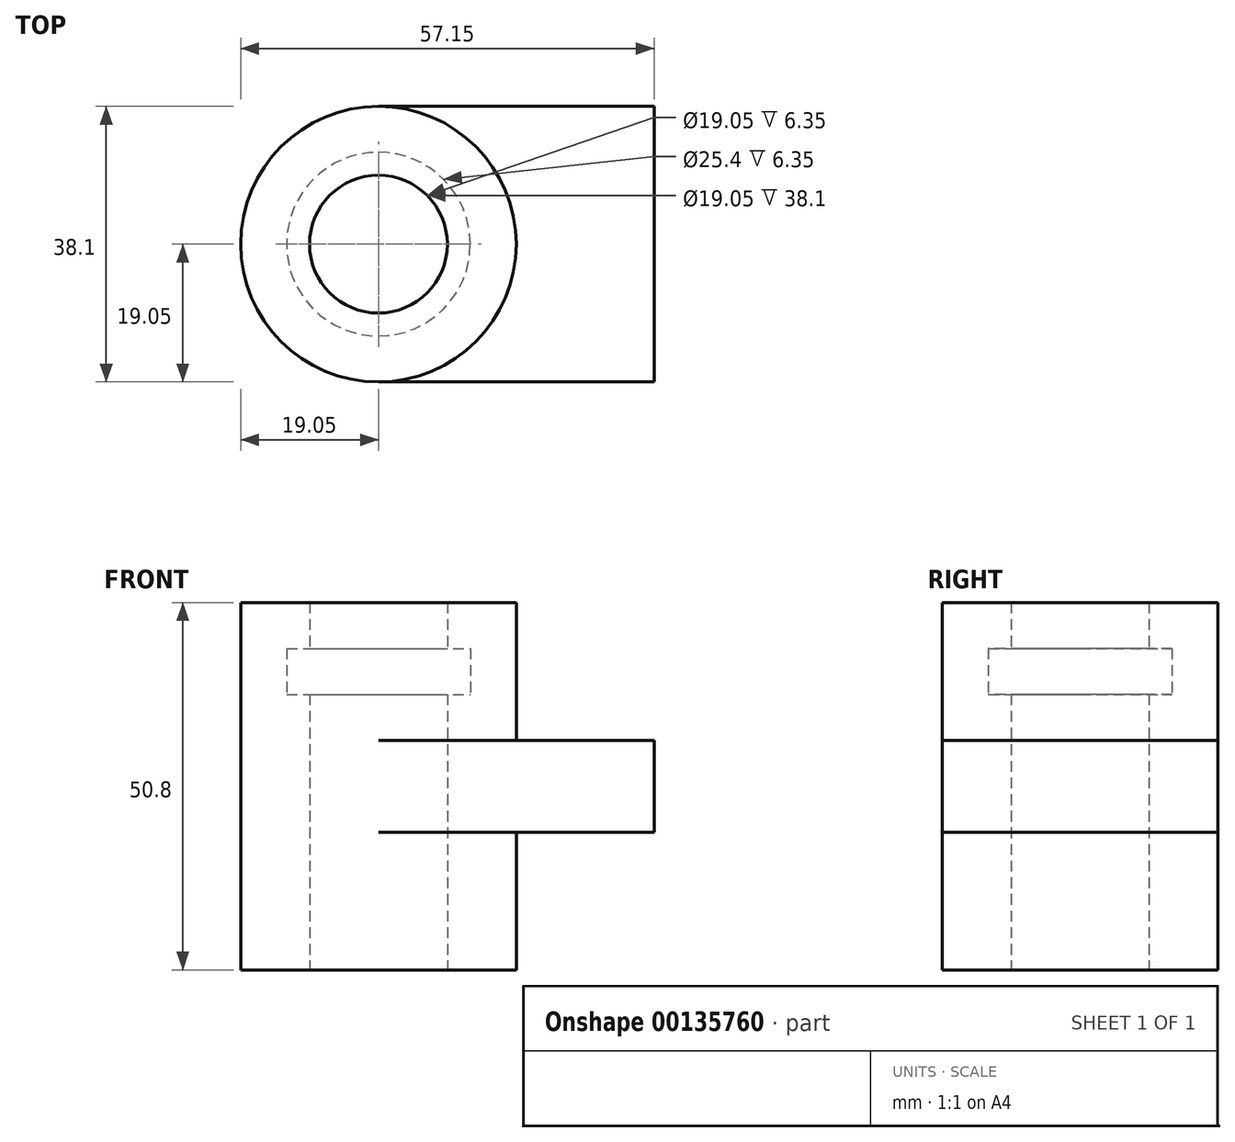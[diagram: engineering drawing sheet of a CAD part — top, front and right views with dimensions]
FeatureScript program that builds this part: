
annotation { "Feature Type Name" : "Feature", "Feature Type Description" : "" }
export const myFeature = defineFeature(function(context is Context, id is Id, definition is map)
    precondition{}
    {
        {
            var Q0;
            Q0=qCreatedBy(makeId("Front.planeOp"),FACE);
            var sketch = newSketch(context, id + "F0", { "sketchPlane" : qUnion([Q0])});
            skLineSegment(sketch, "E0", {"start": v(9.53, 0) * mm, "end": v(9.53, 38.1) * mm});
            skLineSegment(sketch, "E1", {"start": v(19.05, 50.8) * mm, "end": v(9.53, 50.8) * mm});
            skLineSegment(sketch, "E2", {"start": v(9.53, 50.8) * mm, "end": v(9.53, 44.45) * mm});
            skLineSegment(sketch, "E3", {"start": v(9.53, 44.45) * mm, "end": v(12.7, 44.45) * mm});
            skLineSegment(sketch, "E4", {"start": v(12.7, 44.45) * mm, "end": v(12.7, 38.1) * mm});
            skLineSegment(sketch, "E5", {"start": v(12.7, 38.1) * mm, "end": v(9.53, 38.1) * mm});
            skLineSegment(sketch, "E6", {"start": v(9.53, 0) * mm, "end": v(19.05, 0) * mm});
            skLineSegment(sketch, "E7", {"start": v(0, 0) * mm, "end": v(0, 37.87) * mm, "construction": true});
            skLineSegment(sketch, "E8", {"start": v(19.05, 50.8) * mm, "end": v(19.05, 0) * mm});
            skLineSegment(sketch, "E9", {"start": v(9.53, 0) * mm, "end": v(0, 0) * mm, "construction": true});
            skSolve(sketch);
        }
        {
            var Q0;
            Q0=makeQuery(id+"F0.imprint","IMPRINT",FACE,{"disambiguationData":[TD([[makeQuery(id+"F0.imprint","IMPRINT",EDGE,{"derivedFrom":sQuery(id+"F0.wireOp",EDGE,"E0")}),-1.0]])]});
            var Q1;
            Q1 = qConstructionFilter(qBodyType(qCreatedBy(id + "F0" ,EDGE), BodyType.WIRE), ConstructionObject.NO);
            var Q2;
            Q2=sQuery(id+"F0.wireOp",EDGE,"E7");
            revolve(context, id + "F1", {"entities" : qUnion([Q0]), "surfaceEntities" : qUnion([Q1]), "axis" : qUnion([Q2]), "revolveType" : RevolveType.FULL});
        }
        {
            var Q0;
            Q0=qCreatedBy(makeId("Right.planeOp"),FACE);
            var Q1;
            Q1 = qBodyType(qCreatedBy(id + "F3" ,EDGE), BodyType.WIRE);
            cPlane(context, id + "F2", {"entities" : qUnion([Q0, Q1]), "cplaneType" : CPlaneType.OFFSET, "offset" : 38.1 * mm, "width" : 152.4 * mm, "height" : 152.4 * mm});
        }
        {
            var Q0;
            Q0=qCreatedBy(id+"F2.planeOp",FACE);
            var sketch = newSketch(context, id + "F3", { "sketchPlane" : qUnion([Q0])});
            skLineSegment(sketch, "E10.bottom", {"start": v(19.05, 31.75) * mm, "end": v(-19.05, 31.75) * mm});
            skLineSegment(sketch, "E10.top", {"start": v(19.05, 19.05) * mm, "end": v(-19.05, 19.05) * mm});
            skLineSegment(sketch, "E10.left", {"start": v(19.05, 31.75) * mm, "end": v(19.05, 19.05) * mm});
            skLineSegment(sketch, "E10.right", {"start": v(-19.05, 31.75) * mm, "end": v(-19.05, 19.05) * mm});
            skSolve(sketch);
        }
        {
            var Q0;
            Q0=makeQuery(id+"F3.imprint","IMPRINT",FACE,{"disambiguationData":[TD([[makeQuery(id+"F3.imprint","IMPRINT",EDGE,{"derivedFrom":sQuery(id+"F3.wireOp",EDGE,"E10.bottom")}),1.0]])]});
            extrude(context, id + "F4", {"entities" : qUnion([Q0]), "operationType" : NewBodyOperationType.ADD, "endBound" : BoundingType.UP_TO_NEXT, "oppositeDirection" : true, "depth" : 25.4 * mm});
        }
    });
